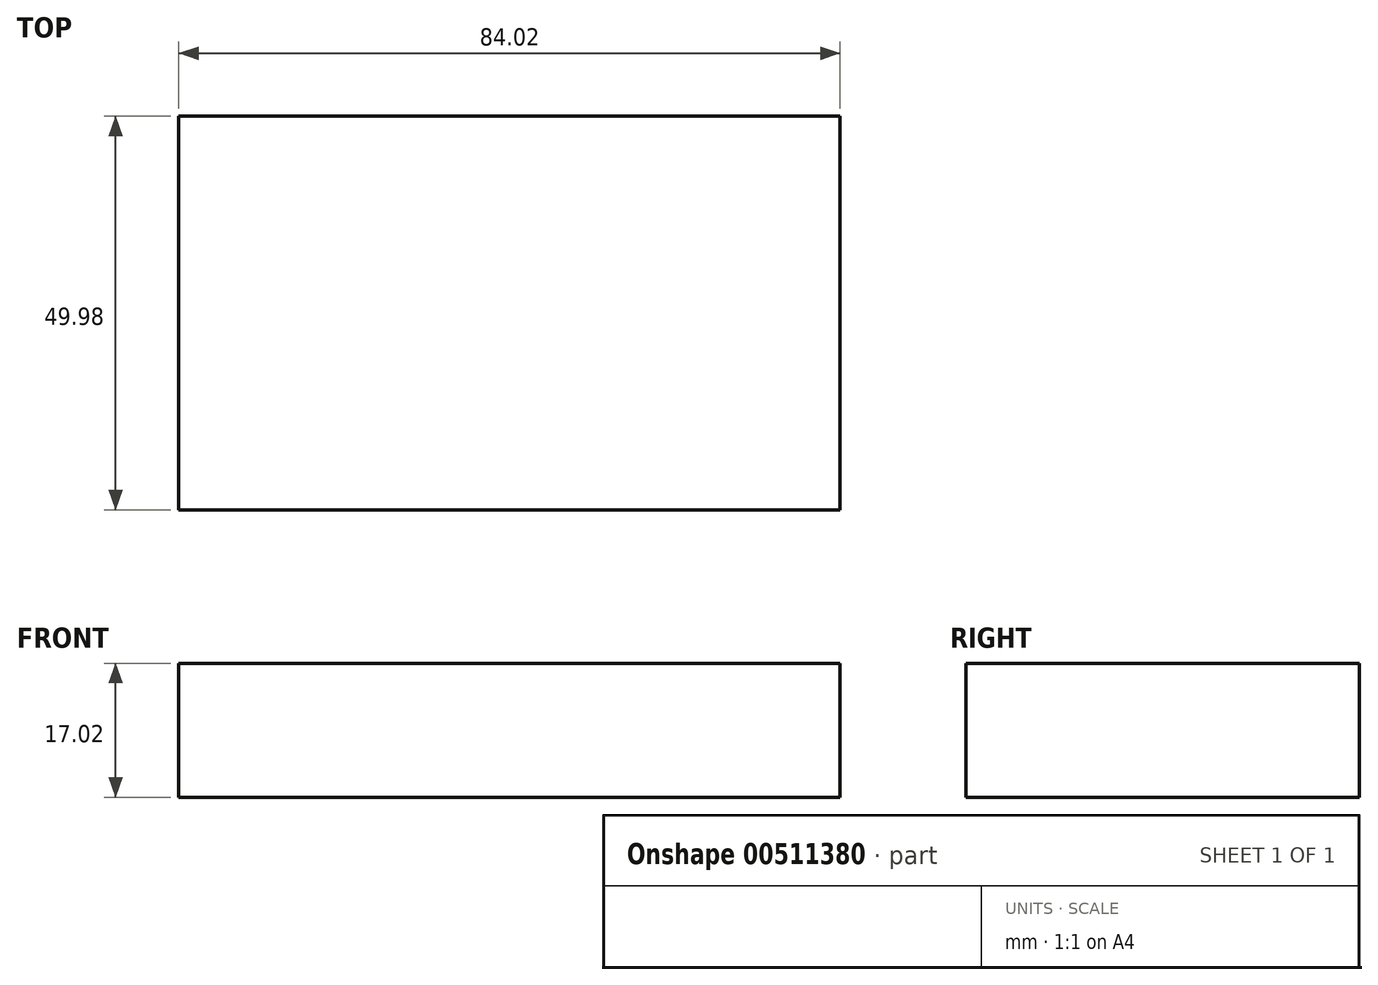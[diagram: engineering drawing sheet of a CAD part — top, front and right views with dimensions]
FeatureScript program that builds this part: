
annotation { "Feature Type Name" : "Feature", "Feature Type Description" : "" }
export const myFeature = defineFeature(function(context is Context, id is Id, definition is map)
    precondition{}
    {
        {
            var Q0;
            Q0=qCreatedBy(makeId("Top.planeOp"),FACE);
            var sketch = newSketch(context, id + "F0", { "sketchPlane" : qUnion([Q0])});
            skLineSegment(sketch, "E0.bottom", {"start": v(-42.01, 25) * mm, "end": v(42.01, 25) * mm});
            skLineSegment(sketch, "E0.top", {"start": v(-42.01, -25) * mm, "end": v(42.01, -25) * mm});
            skLineSegment(sketch, "E0.left", {"start": v(-42.01, 25) * mm, "end": v(-42.01, -25) * mm});
            skLineSegment(sketch, "E0.right", {"start": v(42.01, 25) * mm, "end": v(42.01, -25) * mm});
            skPoint(sketch, "E0.middle", {"position": v(0, 0) * mm});
            skSolve(sketch);
        }
        {
            var Q0;
            Q0=makeQuery(id+"F0.imprint","IMPRINT",FACE,{"disambiguationData":[TD([[makeQuery(id+"F0.imprint","IMPRINT",EDGE,{"derivedFrom":sQuery(id+"F0.wireOp",EDGE,"E0.bottom")}),-1.0]])]});
            extrude(context, id + "F1", {"entities" : qUnion([Q0]), "endBound" : BoundingType.SYMMETRIC, "depth" : 17.02 * mm, "offsetDistance" : 25.4 * mm});
        }
    });
